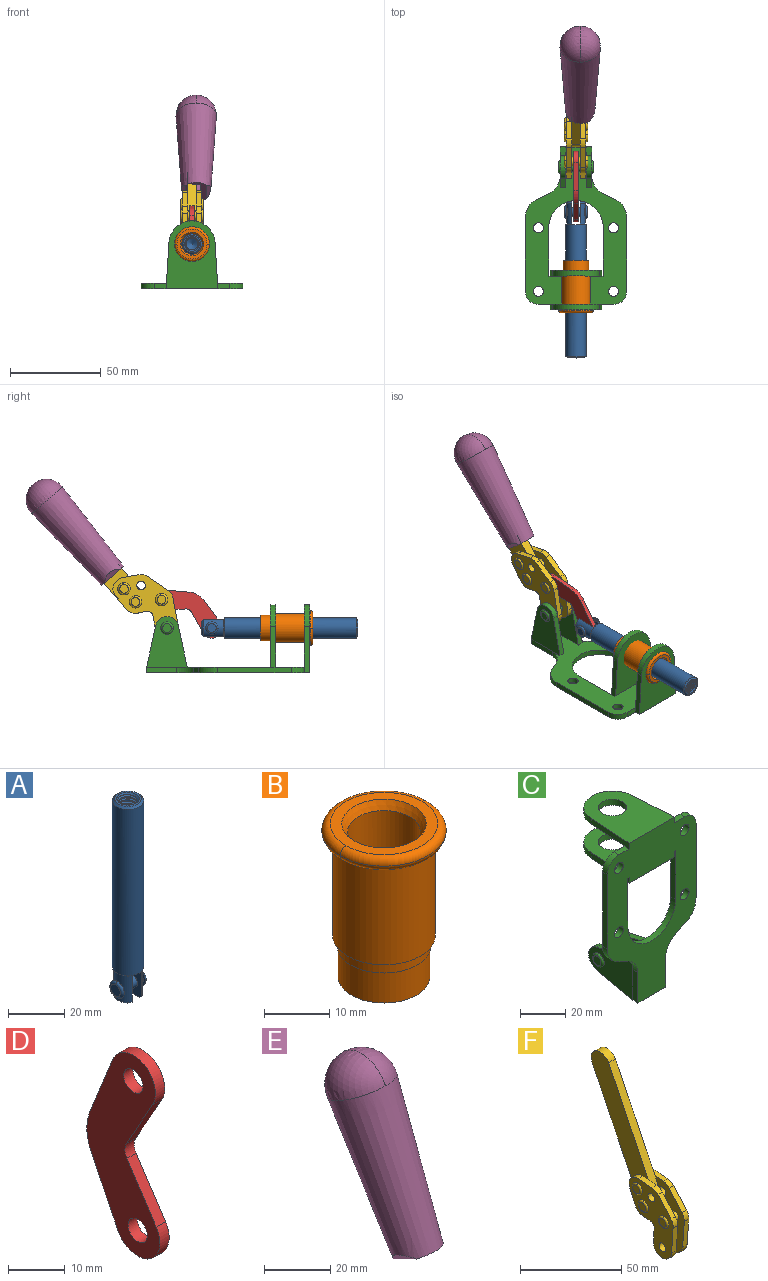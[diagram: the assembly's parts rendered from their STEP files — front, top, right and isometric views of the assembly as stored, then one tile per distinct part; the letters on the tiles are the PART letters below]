
ASSEMBLY  parts=6 mates=6
PART A: 48 faces, bbox 12.6x11.1x86.1 mm
  f0: torus R=2.41mm, axis (-1,0,0), area 15mm2, adj f30,f32,f34
  f1: torus R=2.41mm, axis (-1,0,0), area 15mm2, adj f29,f31,f33
  f2: cylinder r=5.54mm len=72.39mm, axis (0,0,1), area 2518.5mm2, adj f3,f4,f42,f43
  f3: cone r=5.54mm half-angle=45deg, axis (0,0,1), area 7.6mm2, adj f2,f5,f41
  f4: cone r=5.54mm half-angle=45deg, axis (0,0,-1), area 34.9mm2, adj f2,f39
  f5: cylinder r=5.08mm len=11.48mm, axis (0,0,1), area 108.3mm2, adj f3,f7,f8,f41
  f6: cylinder r=2.41mm len=4.83mm, axis (-1,0,0), area 71.2mm2, adj f40,f41
  f7: cylinder r=2.41mm len=4.83mm, axis (-1,0,0), area 7.6mm2, adj f5,f34
  f8: cone r=5.08mm half-angle=45deg, axis (0,0,1), area 10.6mm2, adj f5,f37,f41
  f9: cone r=3.98mm half-angle=45deg, axis (0,0,1), area 17.6mm2, adj f27,f39,f45,f46,f47
  f10: cylinder r=2.41mm len=4.83mm, axis (-1,0,0), area 7.6mm2, adj f33,f38
  f11: cylinder r=3.2mm len=6.4mm, axis (0,0,1), area 78.4mm2, adj f12,f28,f44,f45,f47
  f12: cylinder r=3.2mm len=6.4mm, axis (0,0,1), area 10.5mm2, adj f11,f13,f45,f47
  f13: cylinder r=3.2mm len=6.4mm, axis (0,0,1), area 10.5mm2, adj f12,f14,f45,f47
  f14: cylinder r=3.2mm len=6.4mm, axis (0,0,1), area 10.5mm2, adj f13,f15,f45,f47
  f15: cylinder r=3.2mm len=6.4mm, axis (0,0,1), area 10.5mm2, adj f14,f16,f45,f47
  f16: cylinder r=3.2mm len=6.4mm, axis (0,0,1), area 10.5mm2, adj f15,f17,f45,f47
  f17: cylinder r=3.2mm len=6.4mm, axis (0,0,1), area 10.5mm2, adj f16,f18,f45,f47
  f18: cylinder r=3.2mm len=6.4mm, axis (0,0,1), area 10.5mm2, adj f17,f19,f45,f47
  f19: cylinder r=3.2mm len=6.4mm, axis (0,0,1), area 10.5mm2, adj f18,f20,f45,f47
  f20: cylinder r=3.2mm len=6.4mm, axis (0,0,1), area 10.5mm2, adj f19,f21,f45,f47
  f21: cylinder r=3.2mm len=6.4mm, axis (0,0,1), area 10.5mm2, adj f20,f22,f45,f47
  f22: cylinder r=3.2mm len=6.4mm, axis (0,0,1), area 10.5mm2, adj f21,f23,f45,f47
  f23: cylinder r=3.2mm len=6.4mm, axis (0,0,1), area 10.5mm2, adj f22,f24,f45,f47
  f24: cylinder r=3.2mm len=6.4mm, axis (0,0,1), area 10.5mm2, adj f23,f25,f45,f47
  f25: cylinder r=3.2mm len=6.4mm, axis (0,0,1), area 10.5mm2, adj f24,f26,f45,f47
  f26: cylinder r=3.2mm len=6.4mm, axis (0,0,1), area 10.5mm2, adj f25,f27,f45,f47
  f27: cylinder r=3.2mm len=6.4mm, axis (0,0,1), area 7.4mm2, adj f9,f26,f45,f47
  f28: cone r=3.2mm half-angle=60deg, axis (0,0,1), area 37.2mm2, adj f11
  f29: plane 4.83x4.83mm, normal (-1,0,0), area 18.3mm2, adj f1,f31
  f30: plane 4.83x4.83mm, normal (1,0,0), area 18.3mm2, adj f0,f32
  f31: torus R=2.41mm, axis (-1,0,0), area 15mm2, adj f1,f29,f33
  f32: torus R=2.41mm, axis (-1,0,0), area 15mm2, adj f0,f30,f34
  f33: plane 6.83x6.83mm, normal (1,0,0), area 18.3mm2, adj f1,f10,f31
  f34: plane 6.83x6.83mm, normal (-1,0,0), area 18.3mm2, adj f0,f7,f32
  f35: cone r=5.08mm half-angle=45deg, axis (0,0,1), area 10.6mm2, adj f36,f38,f40
  f36: plane 7.25x1.97mm, normal (0,0,-1), area 10mm2, adj f35,f40
  f37: plane 7.25x1.97mm, normal (0,0,-1), area 10mm2, adj f8,f41
  f38: cylinder r=5.08mm len=11.48mm, axis (0,0,1), area 108.3mm2, adj f10,f35,f40,f42
  f39: plane 9.55x9.55mm, normal (0,0,1), area 22mm2, adj f4,f9
  f40: plane 12.76x10.09mm, normal (1,0,0), area 95.7mm2, adj f6,f35,f36,f38,f42,f43
  f41: plane 12.76x10.09mm, normal (-1,0,0), area 95.7mm2, adj f3,f5,f6,f8,f37,f43
  f42: cone r=5.54mm half-angle=45deg, axis (0,0,1), area 7.6mm2, adj f2,f38,f40
  f43: plane 11.07x4.7mm, normal (0,0,-1), area 50.4mm2, adj f2,f40,f41
  f44: plane 0.89x0.62mm, normal (-1,0,0), area 0.3mm2, adj f11,f45,f46,f47
  f45: bspline ~24.8x7.63mm, area 266.6mm2, adj f9,f11,f12,f13,f14,f15,f16,f17
  f46: bspline ~24.87x7.63mm, area 73.6mm2, adj f9,f44,f45,f47
  f47: bspline ~24.98x7.63mm, area 272.5mm2, adj f9,f11,f12,f13,f14,f15,f16,f17
PART B: 15 faces, bbox 20.6x20.6x28.7 mm
  f0: torus R=8.26mm, axis (0,0,1), area 56.8mm2, adj f1,f10,f12
  f1: torus R=8.26mm, axis (0,0,1), area 56.8mm2, adj f0,f6,f13
  f2: cylinder r=5.59mm len=25.91mm, axis (0,0,1), area 909.6mm2, adj f3,f4
  f3: cone r=6.86mm half-angle=45deg, axis (0,0,-1), area 70.2mm2, adj f2,f14
  f4: cone r=6.47mm half-angle=30deg, axis (0,0,1), area 66.7mm2, adj f2,f13
  f5: cylinder r=7.04mm len=14.07mm, axis (0,0,1), area 252.6mm2, adj f11,f14
  f6: torus R=8.26mm, axis (0,0,1), area 56.8mm2, adj f1,f12,f13
  f7: cylinder r=7.16mm len=14.33mm, axis (0,0,1), area 91.5mm2, adj f9,f11
  f8: cylinder r=7.86mm len=18.42mm, axis (0,0,1), area 909.6mm2, adj f9,f10
  f9: plane 15.72x15.72mm, normal (0,0,-1), area 33mm2, adj f7,f8
  f10: plane 16.51x16.51mm, normal (0,0,-1), area 19.9mm2, adj f0,f8,f12
  f11: plane 14.33x14.33mm, normal (0,0,-1), area 5.7mm2, adj f5,f7
  f12: torus R=8.26mm, axis (0,0,1), area 56.8mm2, adj f0,f6,f10
  f13: plane 16.51x16.51mm, normal (0,0,1), area 82.7mm2, adj f1,f4,f6
  f14: plane 14.07x14.07mm, normal (0,0,-1), area 7.8mm2, adj f3,f5
PART C: 55 faces, bbox 55.7x37.4x89.8 mm
  f0: torus R=2.41mm, axis (-1,0,0), area 15mm2, adj f11,f15,f25
  f1: torus R=2.41mm, axis (-1,0,0), area 15mm2, adj f10,f12,f22
  f2: cylinder r=2.78mm len=5.56mm, axis (0,-1,0), area 54.2mm2, adj f30,f54
  f3: cylinder r=14.99mm len=29.97mm, axis (0,-1,0), area 145.9mm2, adj f30,f49,f53,f54
  f4: cylinder r=2.78mm len=5.56mm, axis (0,-1,0), area 54.2mm2, adj f30,f54
  f5: cylinder r=2.78mm len=5.56mm, axis (0,-1,0), area 54.2mm2, adj f30,f54
  f6: cylinder r=2.78mm len=5.56mm, axis (0,-1,0), area 54.2mm2, adj f30,f54
  f7: cylinder r=6.35mm len=12.7mm, axis (0,0,1), area 123.6mm2, adj f27,f51
  f8: cylinder r=6.35mm len=12.7mm, axis (0,0,-1), area 124.7mm2, adj f21,f35
  f9: cylinder r=2.41mm len=11.18mm, axis (-1,0,0), area 169.4mm2, adj f16,f19
  f10: plane 4.83x4.83mm, normal (1,0,0), area 18.3mm2, adj f1,f12
  f11: plane 4.83x4.83mm, normal (-1,0,0), area 18.3mm2, adj f0,f15
  f12: torus R=2.41mm, axis (-1,0,0), area 15mm2, adj f1,f10,f22
  f13: cylinder r=6.35mm len=12.41mm, axis (1,0,0), area 53.4mm2, adj f18,f19,f22,f23
  f14: cylinder r=6.35mm len=12.41mm, axis (-1,0,0), area 53.4mm2, adj f16,f17,f24,f25
  f15: torus R=2.41mm, axis (-1,0,0), area 15mm2, adj f0,f11,f25
  f16: plane 27.86x22.35mm, normal (1,0,0), area 425.4mm2, adj f9,f14,f17,f24,f30
  f17: plane 22.86x4.97mm, normal (0,0.21,0.98), area 72.5mm2, adj f14,f16,f25,f30
  f18: plane 22.86x4.97mm, normal (0,0.21,0.98), area 72.5mm2, adj f13,f19,f22,f30
  f19: plane 27.86x22.35mm, normal (-1,0,0), area 425.4mm2, adj f9,f13,f18,f23,f30
  f20: cylinder r=12.7mm len=25.35mm, axis (0,0,-1), area 119.8mm2, adj f21,f34,f35,f36
  f21: plane 34.21x28.07mm, normal (0,0,-1), area 702.4mm2, adj f8,f20,f30,f34,f36
  f22: plane 27.96x22.45mm, normal (1,0,0), area 407.2mm2, adj f1,f12,f13,f18,f23,f30,f42,f43
  f23: plane 22.86x4.97mm, normal (0,0.21,-0.98), area 72.5mm2, adj f13,f19,f22,f44
  f24: plane 22.86x4.97mm, normal (0,0.21,-0.98), area 72.5mm2, adj f14,f16,f25,f44
  f25: plane 27.86x22.35mm, normal (-1,0,0), area 407.1mm2, adj f0,f14,f15,f17,f24,f30,f45,f46
  f26: plane 3.1x0.95mm, normal (0,0,-1), area 2.7mm2, adj f30,f49,f50,f54
  f27: plane 34.21x28.07mm, normal (0,0,1), area 702.4mm2, adj f7,f28,f30,f50,f52
  f28: cylinder r=12.7mm len=25.35mm, axis (0,0,1), area 118.8mm2, adj f27,f50,f51,f52
  f29: plane 3.1x0.95mm, normal (0,0,-1), area 2.7mm2, adj f30,f52,f53,f54
  f30: plane 86.54x55.63mm, normal (0,1,0), area 2362.9mm2, adj f2,f3,f4,f5,f6,f16,f17,f18
  f31: plane 40.56x3.1mm, normal (-1,0,0), area 125.7mm2, adj f30,f32,f48,f54
  f32: cylinder r=7.11mm len=7.11mm, axis (0,-1,0), area 34.6mm2, adj f30,f31,f33,f54
  f33: plane 6.67x3.1mm, normal (0,0,1), area 20.4mm2, adj f30,f32,f34,f54
  f34: plane 25.39x3.13mm, normal (-1,0.06,0), area 79.5mm2, adj f20,f21,f33,f35,f54
  f35: plane 37.31x28.45mm, normal (0,0,1), area 789.9mm2, adj f8,f20,f34,f36,f54
  f36: plane 25.39x3.13mm, normal (1,0.06,0), area 79.5mm2, adj f20,f21,f35,f37,f54
  f37: plane 6.67x3.1mm, normal (0,0,1), area 20.4mm2, adj f30,f36,f38,f54
  f38: cylinder r=7.11mm len=7.11mm, axis (0,-1,0), area 34.6mm2, adj f30,f37,f39,f54
  f39: plane 40.56x3.1mm, normal (1,0,0), area 125.7mm2, adj f30,f38,f40,f54
  f40: cylinder r=11.18mm len=10.16mm, axis (0,-1,0), area 39.5mm2, adj f30,f39,f41,f54
  f41: plane 6.09x3.1mm, normal (0.42,0,-0.91), area 20.8mm2, adj f30,f40,f42,f54
  f42: cylinder r=11.18mm len=9.41mm, axis (0,-1,0), area 37.2mm2, adj f22,f30,f41,f43,f54
  f43: plane 16.5x3.1mm, normal (1,0,0), area 51.1mm2, adj f22,f42,f44,f54
  f44: plane 17.37x3.1mm, normal (0,0,-1), area 53.8mm2, adj f23,f24,f30,f43,f45,f54
  f45: plane 16.5x3.1mm, normal (-1,0,0), area 51.1mm2, adj f25,f44,f46,f54
  f46: cylinder r=11.18mm len=9.41mm, axis (0,-1,0), area 37.2mm2, adj f25,f30,f45,f47,f54
  f47: plane 6.09x3.1mm, normal (-0.42,0,-0.91), area 20.8mm2, adj f30,f46,f48,f54
  f48: cylinder r=11.18mm len=10.16mm, axis (0,-1,0), area 39.5mm2, adj f30,f31,f47,f54
  f49: plane 26.54x3.1mm, normal (-1,0,0), area 82.3mm2, adj f3,f26,f30,f54
  f50: plane 25.39x3.1mm, normal (1,0.06,0), area 78.8mm2, adj f26,f27,f28,f51,f54
  f51: plane 37.31x28.45mm, normal (0,0,-1), area 789.9mm2, adj f7,f28,f50,f52,f54
  f52: plane 25.39x3.1mm, normal (-1,0.06,0), area 78.8mm2, adj f27,f28,f29,f51,f54
  f53: plane 26.54x3.1mm, normal (1,0,0), area 82.3mm2, adj f3,f29,f30,f54
  f54: plane 89.66x55.63mm, normal (0,-1,0), area 2678.5mm2, adj f2,f3,f4,f5,f6,f26,f29,f31
PART D: 12 faces, bbox 2.3x18.2x42.8 mm
  f0: cylinder r=2.4mm len=4.8mm, axis (1,0,0), area 34.9mm2, adj f4,f11
  f1: cylinder r=10.41mm len=8.47mm, axis (1,0,0), area 20.2mm2, adj f4,f9,f10,f11
  f2: cylinder r=3.05mm len=3.16mm, axis (1,0,0), area 7.7mm2, adj f4,f6,f7,f11
  f3: cylinder r=2.4mm len=4.8mm, axis (1,0,0), area 34.9mm2, adj f4,f11
  f4: plane 42.81x18.23mm, normal (-1,0,0), area 414.1mm2, adj f0,f1,f2,f3,f5,f6,f7,f8
  f5: cylinder r=5.54mm len=10.67mm, axis (1,0,0), area 41.8mm2, adj f4,f6,f10,f11
  f6: plane 11.66x6.53mm, normal (0,-0.87,-0.49), area 30.9mm2, adj f2,f4,f5,f11
  f7: plane 11.17x7.33mm, normal (0,-0.84,0.55), area 30.9mm2, adj f2,f4,f8,f11
  f8: cylinder r=5.54mm len=10.51mm, axis (1,0,0), area 41.8mm2, adj f4,f7,f9,f11
  f9: plane 13.67x6.67mm, normal (0,0.9,-0.44), area 35.1mm2, adj f1,f4,f8,f11
  f10: plane 14.1x5.7mm, normal (0,0.93,0.37), area 35.1mm2, adj f1,f4,f5,f11
  f11: plane 42.81x18.23mm, normal (1,0,0), area 414.1mm2, adj f0,f1,f2,f3,f5,f6,f7,f8
PART E: 11 faces, bbox 22.3x42.6x64.5 mm
  f0: sphere r=11.13mm, area 411.4mm2, adj f1,f8
  f1: cone r=11.11mm half-angle=3.3deg, axis (0,0.44,0.9), area 3251.8mm2, adj f0,f7,f8,f9,f10
  f2: cylinder r=6.16mm len=11.7mm, axis (1,0,0), area 89.5mm2, adj f3,f4,f5,f6
  f3: plane 60.23x36.75mm, normal (-1,0,0), area 763.6mm2, adj f2,f4,f6,f10
  f4: plane 51.37x25.05mm, normal (0,0.9,-0.44), area 264.2mm2, adj f2,f3,f5,f10
  f5: plane 60.23x36.75mm, normal (1,0,0), area 763.6mm2, adj f2,f4,f6,f10
  f6: plane 51.37x25.05mm, normal (0,-0.9,0.44), area 264.2mm2, adj f2,f3,f5,f10
  f7: plane 9.95x5.95mm, normal (0.71,-0.31,-0.64), area 25.8mm2, adj f1,f10
  f8: sphere r=11.13mm, area 411.4mm2, adj f0,f1
  f9: plane 9.95x5.95mm, normal (-0.71,-0.31,-0.64), area 25.8mm2, adj f1,f10
  f10: plane 14.27x11.38mm, normal (0,-0.44,-0.9), area 106.7mm2, adj f1,f3,f4,f5,f6,f7,f9
PART F: 59 faces, bbox 12.9x60.2x99.6 mm
  f0: torus R=2.39mm, axis (-1,0,0), area 14.9mm2, adj f20,f43,f51
  f1: torus R=2.39mm, axis (-1,0,0), area 14.9mm2, adj f19,f42,f51
  f2: torus R=2.39mm, axis (-1,0,0), area 14.9mm2, adj f18,f35,f51
  f3: torus R=2.39mm, axis (-1,0,0), area 14.9mm2, adj f14,f17,f23
  f4: torus R=2.39mm, axis (-1,0,0), area 14.9mm2, adj f13,f16,f23
  f5: torus R=2.39mm, axis (-1,0,0), area 14.9mm2, adj f12,f15,f23
  f6: cylinder r=2.39mm len=4.78mm, axis (1,0,0), area 46.5mm2, adj f48,f50,f51
  f7: cylinder r=2.39mm len=4.78mm, axis (1,0,0), area 46.5mm2, adj f50,f51
  f8: cylinder r=6.35mm len=12.68mm, axis (1,0,0), area 61.8mm2, adj f38,f39,f50,f51
  f9: cylinder r=2.39mm len=4.78mm, axis (-1,0,0), area 70.5mm2, adj f46,f50
  f10: cylinder r=2.39mm len=4.78mm, axis (-1,0,0), area 46.5mm2, adj f23,f45,f46
  f11: cylinder r=2.39mm len=4.78mm, axis (-1,0,0), area 46.5mm2, adj f23,f46
  f12: plane 4.78x4.78mm, normal (1,0,0), area 17.9mm2, adj f5,f15
  f13: plane 4.78x4.78mm, normal (1,0,0), area 17.9mm2, adj f4,f16
  f14: plane 4.78x4.78mm, normal (1,0,0), area 17.9mm2, adj f3,f17
  f15: torus R=2.39mm, axis (-1,0,0), area 14.9mm2, adj f5,f12,f23
  f16: torus R=2.39mm, axis (-1,0,0), area 14.9mm2, adj f4,f13,f23
  f17: torus R=2.39mm, axis (-1,0,0), area 14.9mm2, adj f3,f14,f23
  f18: plane 4.78x4.78mm, normal (-1,0,0), area 17.9mm2, adj f2,f35
  f19: plane 4.78x4.78mm, normal (-1,0,0), area 17.9mm2, adj f1,f42
  f20: plane 4.78x4.78mm, normal (-1,0,0), area 17.9mm2, adj f0,f43
  f21: plane 2.26x0.2mm, normal (1,0,0), area 0.2mm2, adj f31,f44
  f22: plane 2.26x0.2mm, normal (-1,0,0), area 0.2mm2, adj f41,f44
  f23: plane 39.37x30.77mm, normal (1,0,0), area 565.5mm2, adj f3,f4,f5,f10,f11,f15,f16,f17
  f24: cylinder r=6.1mm len=4.15mm, axis (-1,0,0), area 14.7mm2, adj f23,f25,f32,f46
  f25: plane 10.25x9.01mm, normal (0,-0.75,0.66), area 42.3mm2, adj f23,f24,f26,f46
  f26: cylinder r=6.35mm len=4.64mm, axis (-1,0,0), area 15.6mm2, adj f23,f25,f27,f46
  f27: plane 15.84x3.1mm, normal (0,-1,-0.07), area 49.2mm2, adj f23,f26,f28,f46
  f28: cylinder r=6.35mm len=12.68mm, axis (-1,0,0), area 61.8mm2, adj f23,f27,f29,f46
  f29: plane 8.11x3.1mm, normal (0,1,0.07), area 25.2mm2, adj f23,f28,f30,f46
  f30: cylinder r=3.05mm len=3.25mm, axis (-1,0,0), area 14.8mm2, adj f23,f29,f31,f46
  f31: plane 5.99x3.1mm, normal (0,0.07,-1), area 18.6mm2, adj f21,f23,f30,f44,f46
  f32: plane 9.5x3.1mm, normal (0,-0.07,1), area 29.5mm2, adj f23,f24,f33,f46,f47
  f33: cylinder r=6.1mm len=8.63mm, axis (-1,0,0), area 39.1mm2, adj f23,f32,f34,f47
  f34: plane 8.65x3.96mm, normal (0,0.91,-0.42), area 29.5mm2, adj f23,f33,f44,f47
  f35: torus R=2.39mm, axis (-1,0,0), area 14.9mm2, adj f2,f18,f51
  f36: plane 10.25x9.01mm, normal (0,-0.75,0.66), area 42.3mm2, adj f37,f49,f50,f51
  f37: cylinder r=6.35mm len=4.64mm, axis (1,0,0), area 15.6mm2, adj f36,f38,f50,f51
  f38: plane 15.84x3.1mm, normal (0,-1,-0.07), area 49.2mm2, adj f8,f37,f50,f51
  f39: plane 8.11x3.1mm, normal (0,1,0.07), area 25.2mm2, adj f8,f40,f50,f51
  f40: cylinder r=3.05mm len=3.25mm, axis (1,0,0), area 14.8mm2, adj f39,f41,f50,f51
  f41: plane 5.99x3.1mm, normal (0,0.07,-1), area 18.6mm2, adj f22,f40,f44,f50,f51
  f42: torus R=2.39mm, axis (-1,0,0), area 14.9mm2, adj f1,f19,f51
  f43: torus R=2.39mm, axis (-1,0,0), area 14.9mm2, adj f0,f20,f51
  f44: cylinder r=6.35mm len=12.12mm, axis (-1,0,0), area 128.9mm2, adj f21,f22,f23,f31,f34,f41,f46,f47
  f45: plane 2.65x1.35mm, normal (1,0,0), area 1mm2, adj f10,f55
  f46: plane 39.08x20.42mm, normal (-1,0,0), area 412.5mm2, adj f9,f10,f11,f24,f25,f26,f27,f28
  f47: plane 77.62x39.82mm, normal (1,0,0), area 850mm2, adj f32,f33,f34,f44,f53,f54,f55
  f48: plane 2.65x1.35mm, normal (-1,0,0), area 1mm2, adj f6,f55
  f49: cylinder r=6.1mm len=4.15mm, axis (1,0,0), area 14.7mm2, adj f36,f50,f51,f56
  f50: plane 39.08x20.42mm, normal (1,0,0), area 412.5mm2, adj f6,f7,f8,f9,f36,f37,f38,f39
  f51: plane 39.37x30.77mm, normal (-1,0,0), area 565.5mm2, adj f0,f1,f2,f6,f7,f8,f35,f36
  f52: plane 8.65x3.96mm, normal (0,0.91,-0.42), area 29.5mm2, adj f44,f51,f57,f58
  f53: plane 68.49x33.4mm, normal (0,0.9,-0.44), area 358.1mm2, adj f44,f47,f54,f58
  f54: cylinder r=6.35mm len=12.06mm, axis (1,0,0), area 93.7mm2, adj f47,f53,f55,f58
  f55: plane 68.49x33.4mm, normal (0,-0.9,0.44), area 358.1mm2, adj f44,f45,f46,f47,f48,f50,f54,f58
  f56: plane 9.5x3.1mm, normal (0,-0.07,1), area 29.5mm2, adj f49,f50,f51,f57,f58
  f57: cylinder r=6.1mm len=8.63mm, axis (1,0,0), area 39.1mm2, adj f51,f52,f56,f58
  f58: plane 77.62x39.82mm, normal (-1,0,0), area 850mm2, adj f44,f52,f53,f54,f55,f56,f57
PLACE A rot(axis=(1,0,0),90deg) t=(0,32.07,0)mm
PLACE B rot(axis=(1,0,0),90deg) t=(0,10.16,0)mm
PLACE C rot(axis=(1,0,0),90deg) t=(0,9.14,0)mm fixed
PLACE D rot(axis=(1,0,0),121.4deg) t=(0,42.63,11.66)mm
PLACE E rot(axis=(-1,0,0),15deg) t=(2.31,25.77,61.98)mm
PLACE F rot(axis=(-1,0,0),15deg) t=(0,25.77,61.98)mm
MATE slider A.f2 <-> B.f2  axis (0,-1,0) through (0,-26.71,24.61)mm
MATE revolute D.f3 <-> F.f4  axis (1,0,0) through (0,44.26,40.2)mm
MATE fastened B.f2 <-> C.f7  axis (0,-1,0) through (0,-37.25,24.61)mm
MATE fastened E.f2 <-> F.f54  axis (1,0,0) through (0,108.56,96.5)mm
MATE revolute F.f7 <-> C.f0  axis (1,0,0) through (0,41.23,24.61)mm
MATE revolute D.f5 <-> A.f6  axis (1,0,0) through (0,16.6,24.61)mm
